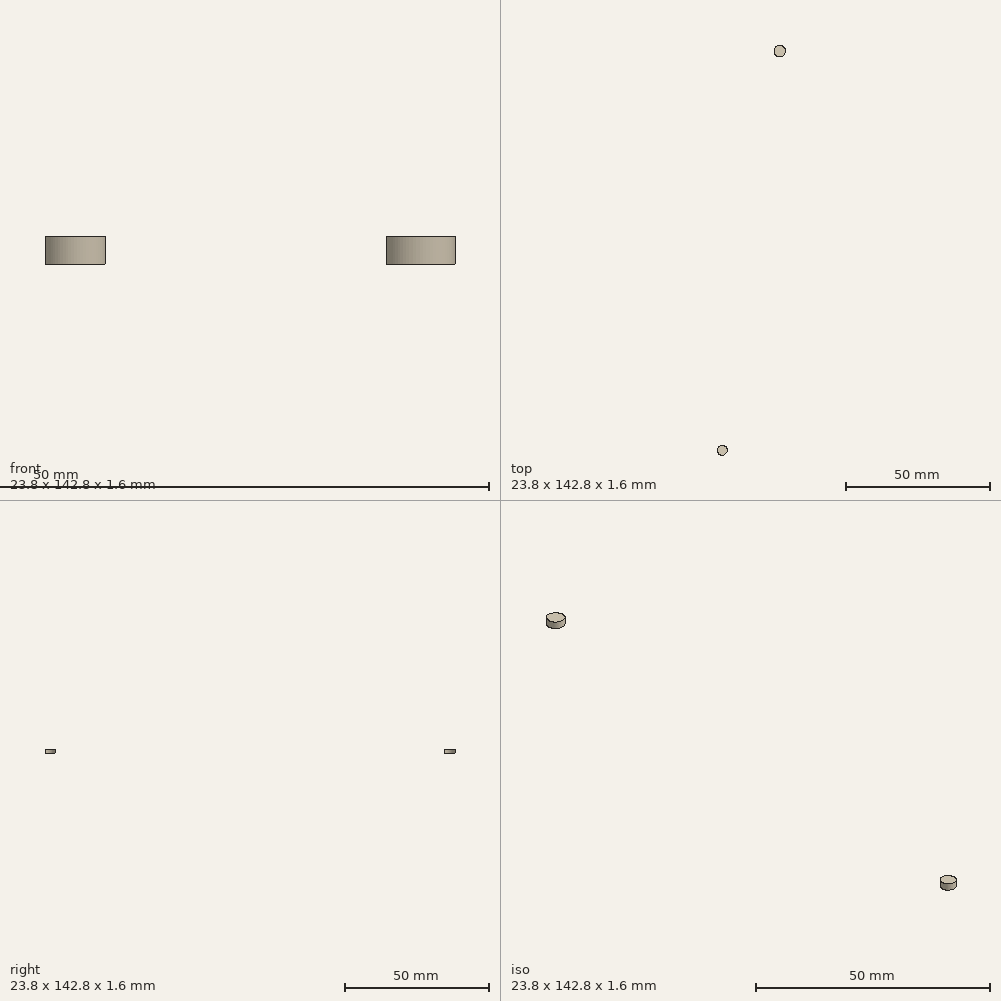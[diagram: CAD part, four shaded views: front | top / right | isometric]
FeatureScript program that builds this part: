
annotation { "Feature Type Name" : "Feature", "Feature Type Description" : "" }
export const myFeature = defineFeature(function(context is Context, id is Id, definition is map)
    precondition{}
    {
        {
            var Q0;
            Q0=qCreatedBy(makeId("Top.planeOp"),FACE);
            var sketch = newSketch(context, id + "F0", { "sketchPlane" : qUnion([Q0])});
            skLineSegment(sketch, "E0.bottom", {"start": v(-60, 75) * mm, "end": v(60, 75) * mm});
            skLineSegment(sketch, "E0.top", {"start": v(-60, -75) * mm, "end": v(60, -75) * mm});
            skLineSegment(sketch, "E0.left", {"start": v(-60, 75) * mm, "end": v(-60, -75) * mm});
            skLineSegment(sketch, "E0.right", {"start": v(60, 75) * mm, "end": v(60, -75) * mm});
            skSolve(sketch);
        }
        {
            var Q0;
            Q0=makeQuery(id+"F0.imprint","IMPRINT",FACE,{"disambiguationData":[TD([[makeQuery(id+"F0.imprint","IMPRINT",EDGE,{"derivedFrom":sQuery(id+"F0.wireOp",EDGE,"E0.bottom")}),-1.0]])]});
            extrude(context, id + "F1", {"entities" : qUnion([Q0]), "depth" : 1.6 * mm, "offsetDistance" : 25 * mm});
        }
        {
            var Q0;
            Q0=makeQuery(id+"F1.opExtrude","CAP_FACE",FACE,{"disambiguationData":[OSD([sQuery(id+"F0.wireOp",EDGE,"E0.bottom"),sQuery(id+"F0.wireOp",EDGE,"E0.top"),sQuery(id+"F0.wireOp",EDGE,"E0.left"),sQuery(id+"F0.wireOp",EDGE,"E0.right")])],"isStart":false});
            var sketch = newSketch(context, id + "F2", { "sketchPlane" : qUnion([Q0])});
            skLineSegment(sketch, "E1", {"start": v(0, 75) * mm, "end": v(0, -75) * mm, "construction": true});
            skLineSegment(sketch, "E2", {"start": v(-60, -70) * mm, "end": v(60, -70) * mm, "construction": true});
            skLineSegment(sketch, "E3", {"start": v(-60, 69) * mm, "end": v(60, 69) * mm, "construction": true});
            skCircle(sketch, "E4", {"center": v(-30, -70) * mm, "radius": 1.75 * mm});
            skCircle(sketch, "E5", {"center": v(0, -70) * mm, "radius": 1.75 * mm});
            skCircle(sketch, "E6", {"center": v(-50, 69) * mm, "radius": 2 * mm});
            skCircle(sketch, "E7.MirrorC", {"center": v(50, 69) * mm, "radius": 2 * mm});
            skCircle(sketch, "E8.MirrorC", {"center": v(30, -70) * mm, "radius": 1.75 * mm});
            skSolve(sketch);
        }
        {
            var Q0;
            Q0=makeQuery(id+"F2.imprint","IMPRINT",FACE,{"disambiguationData":[TD([[makeQuery(id+"F2.imprint","IMPRINT",EDGE,{"derivedFrom":sQuery(id+"F2.wireOp",EDGE,"E6")}),1.0]])]});
            var Q1;
            Q1=makeQuery(id+"F2.imprint","IMPRINT",FACE,{"disambiguationData":[TD([[makeQuery(id+"F2.imprint","IMPRINT",EDGE,{"derivedFrom":sQuery(id+"F2.wireOp",EDGE,"E7.MirrorC")}),-1.0]])]});
            var Q2;
            Q2=makeQuery(id+"F2.imprint","IMPRINT",FACE,{"disambiguationData":[TD([[makeQuery(id+"F2.imprint","IMPRINT",EDGE,{"derivedFrom":sQuery(id+"F2.wireOp",EDGE,"E4")}),1.0]])]});
            var Q3;
            Q3=makeQuery(id+"F2.imprint","IMPRINT",FACE,{"disambiguationData":[TD([[makeQuery(id+"F2.imprint","IMPRINT",EDGE,{"derivedFrom":sQuery(id+"F2.wireOp",EDGE,"E5")}),1.0]])]});
            var Q4;
            Q4=makeQuery(id+"F2.imprint","IMPRINT",FACE,{"disambiguationData":[TD([[makeQuery(id+"F2.imprint","IMPRINT",EDGE,{"derivedFrom":sQuery(id+"F2.wireOp",EDGE,"E8.MirrorC")}),-1.0]])]});
            extrude(context, id + "F3", {"entities" : qUnion([Q0, Q1, Q2, Q3, Q4]), "operationType" : NewBodyOperationType.REMOVE, "endBound" : BoundingType.THROUGH_ALL, "oppositeDirection" : true, "depth" : 25 * mm, "offsetDistance" : 25 * mm});
        }
    });
